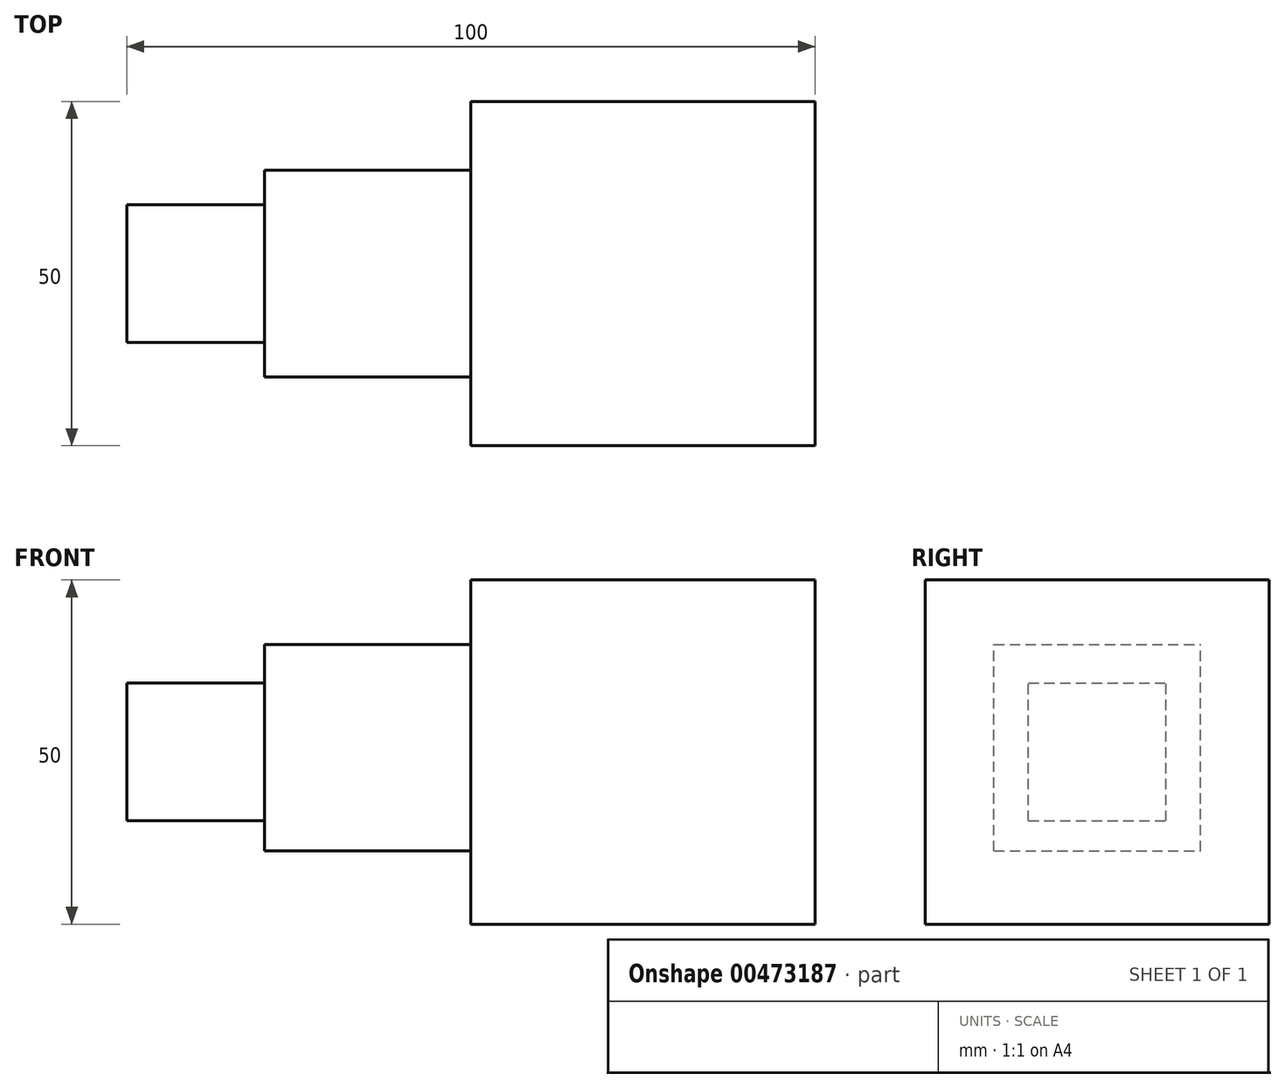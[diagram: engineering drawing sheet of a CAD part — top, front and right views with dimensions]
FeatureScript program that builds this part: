
annotation { "Feature Type Name" : "Feature", "Feature Type Description" : "" }
export const myFeature = defineFeature(function(context is Context, id is Id, definition is map)
    precondition{}
    {
        {
            var Q0;
            Q0=qCreatedBy(makeId("Front.planeOp"),FACE);
            var sketch = newSketch(context, id + "F0", { "sketchPlane" : qUnion([Q0])});
            skLineSegment(sketch, "E0.bottom", {"start": v(-25, 25) * mm, "end": v(25, 25) * mm});
            skLineSegment(sketch, "E0.top", {"start": v(-25, -25) * mm, "end": v(25, -25) * mm});
            skLineSegment(sketch, "E0.left", {"start": v(-25, 25) * mm, "end": v(-25, -25) * mm});
            skLineSegment(sketch, "E0.right", {"start": v(25, 25) * mm, "end": v(25, -25) * mm});
            skSolve(sketch);
        }
        {
            var Q0;
            Q0=makeQuery(id+"F0.imprint","IMPRINT",FACE,{"disambiguationData":[TD([[makeQuery(id+"F0.imprint","IMPRINT",EDGE,{"derivedFrom":sQuery(id+"F0.wireOp",EDGE,"E0.bottom")}),-1.0]])]});
            extrude(context, id + "F1", {"entities" : qUnion([Q0]), "endBound" : BoundingType.SYMMETRIC, "depth" : 50 * mm});
        }
        {
            var Q0;
            Q0=makeQuery(id+"F1.opExtrude","SWEPT_FACE",FACE,{"disambiguationData":[OSD([sQuery(id+"F0.wireOp",EDGE,"E0.left")])]});
            var sketch = newSketch(context, id + "F2", { "sketchPlane" : qUnion([Q0])});
            skLineSegment(sketch, "E1.bottom", {"start": v(15, -14.39) * mm, "end": v(-15, -14.39) * mm});
            skLineSegment(sketch, "E1.top", {"start": v(15, 15.61) * mm, "end": v(-15, 15.61) * mm});
            skLineSegment(sketch, "E1.left", {"start": v(15, -14.39) * mm, "end": v(15, 15.61) * mm});
            skLineSegment(sketch, "E1.right", {"start": v(-15, -14.39) * mm, "end": v(-15, 15.61) * mm});
            skSolve(sketch);
        }
        {
            var Q0;
            Q0 = qSketchRegion(id + "F2", true);
            extrude(context, id + "F3", {"entities" : qUnion([Q0]), "operationType" : NewBodyOperationType.ADD, "depth" : 30 * mm});
        }
        {
            var Q0;
            Q0=makeQuery(id+"F3.opExtrude","CAP_FACE",FACE,{"disambiguationData":[OSD([sQuery(id+"F2.wireOp",EDGE,"E1.bottom"),sQuery(id+"F2.wireOp",EDGE,"E1.top"),sQuery(id+"F2.wireOp",EDGE,"E1.left"),sQuery(id+"F2.wireOp",EDGE,"E1.right")])],"isStart":false});
            var sketch = newSketch(context, id + "F4", { "sketchPlane" : qUnion([Q0])});
            skLineSegment(sketch, "E2.bottom", {"start": v(10, -10) * mm, "end": v(-10, -10) * mm});
            skLineSegment(sketch, "E2.top", {"start": v(10, 10) * mm, "end": v(-10, 10) * mm});
            skLineSegment(sketch, "E2.left", {"start": v(10, -10) * mm, "end": v(10, 10) * mm});
            skLineSegment(sketch, "E2.right", {"start": v(-10, -10) * mm, "end": v(-10, 10) * mm});
            skSolve(sketch);
        }
        {
            var Q0;
            Q0=makeQuery(id+"F4.imprint","IMPRINT",FACE,{"disambiguationData":[TD([[makeQuery(id+"F4.imprint","IMPRINT",EDGE,{"derivedFrom":sQuery(id+"F4.wireOp",EDGE,"E2.bottom")}),-1.0]])]});
            extrude(context, id + "F5", {"entities" : qUnion([Q0]), "operationType" : NewBodyOperationType.ADD, "depth" : 20 * mm});
        }
    });
